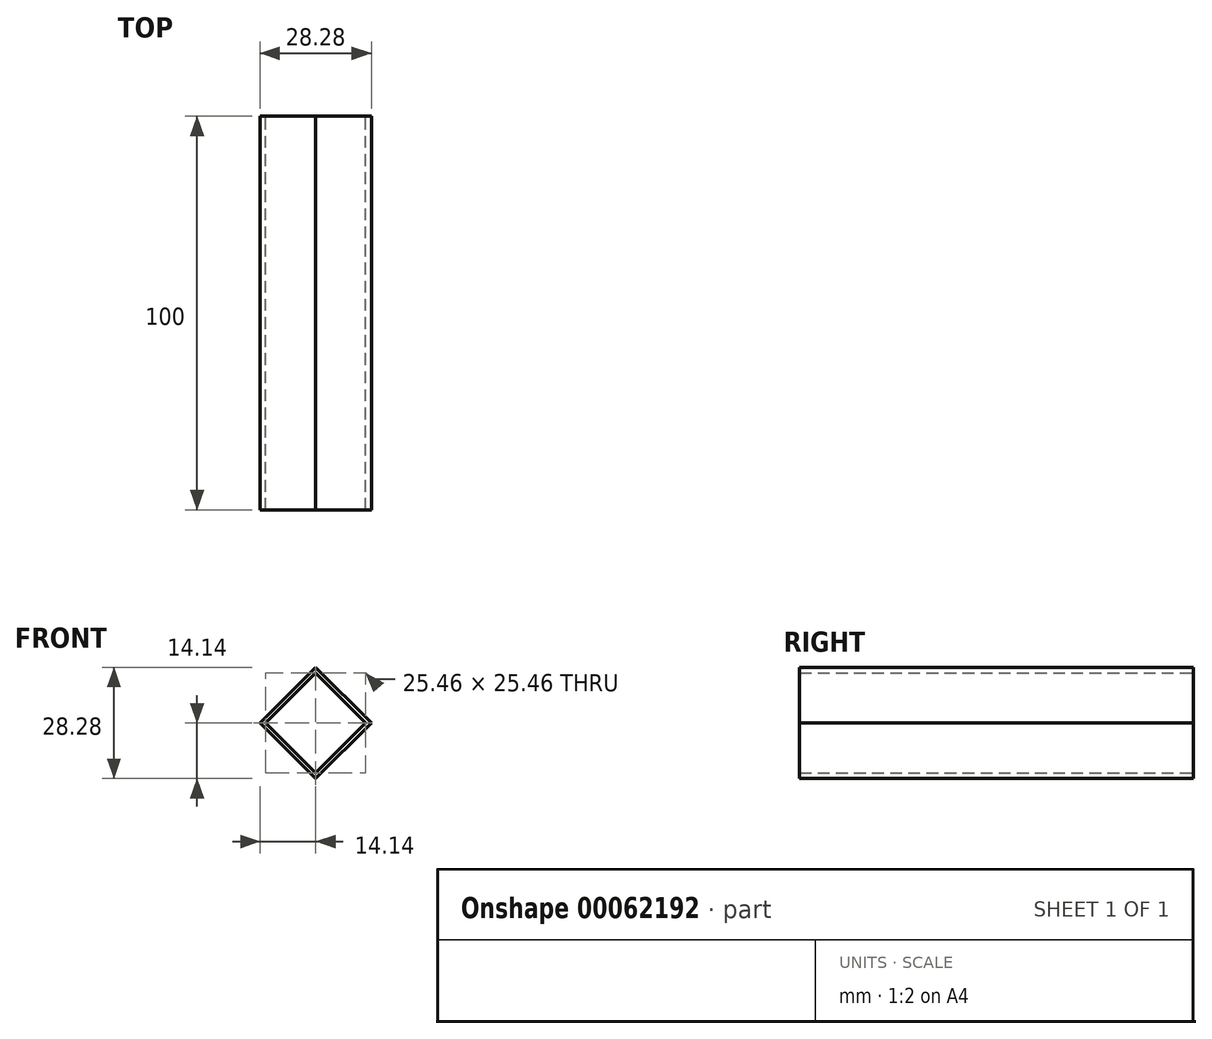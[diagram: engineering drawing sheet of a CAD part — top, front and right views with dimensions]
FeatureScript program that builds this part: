
annotation { "Feature Type Name" : "Feature", "Feature Type Description" : "" }
export const myFeature = defineFeature(function(context is Context, id is Id, definition is map)
    precondition{}
    {
        {
            var Q0;
            Q0=qCreatedBy(makeId("Front.planeOp"),FACE);
            var sketch = newSketch(context, id + "F0", { "sketchPlane" : qUnion([Q0])});
            skLineSegment(sketch, "E0", {"start": v(0, 14.14) * mm, "end": v(-14.14, 0) * mm});
            skLineSegment(sketch, "E1", {"start": v(-14.14, 0) * mm, "end": v(0, -14.14) * mm});
            skLineSegment(sketch, "E2", {"start": v(0, -14.14) * mm, "end": v(14.14, 0) * mm});
            skLineSegment(sketch, "E3", {"start": v(14.14, 0) * mm, "end": v(0, 14.14) * mm});
            skLineSegment(sketch, "E4.0", {"start": v(12.73, 0) * mm, "end": v(0, 12.73) * mm});
            skLineSegment(sketch, "E4.1", {"start": v(0, -12.73) * mm, "end": v(12.73, 0) * mm});
            skLineSegment(sketch, "E4.2", {"start": v(-12.73, 0) * mm, "end": v(0, -12.73) * mm});
            skLineSegment(sketch, "E4.3", {"start": v(0, 12.73) * mm, "end": v(-12.73, 0) * mm});
            skSolve(sketch);
        }
        {
            var Q0;
            Q0 = qSketchRegion(id + "F0", true);
            extrude(context, id + "F1", {"entities" : qUnion([Q0]), "depth" : 100 * mm});
        }
    });
